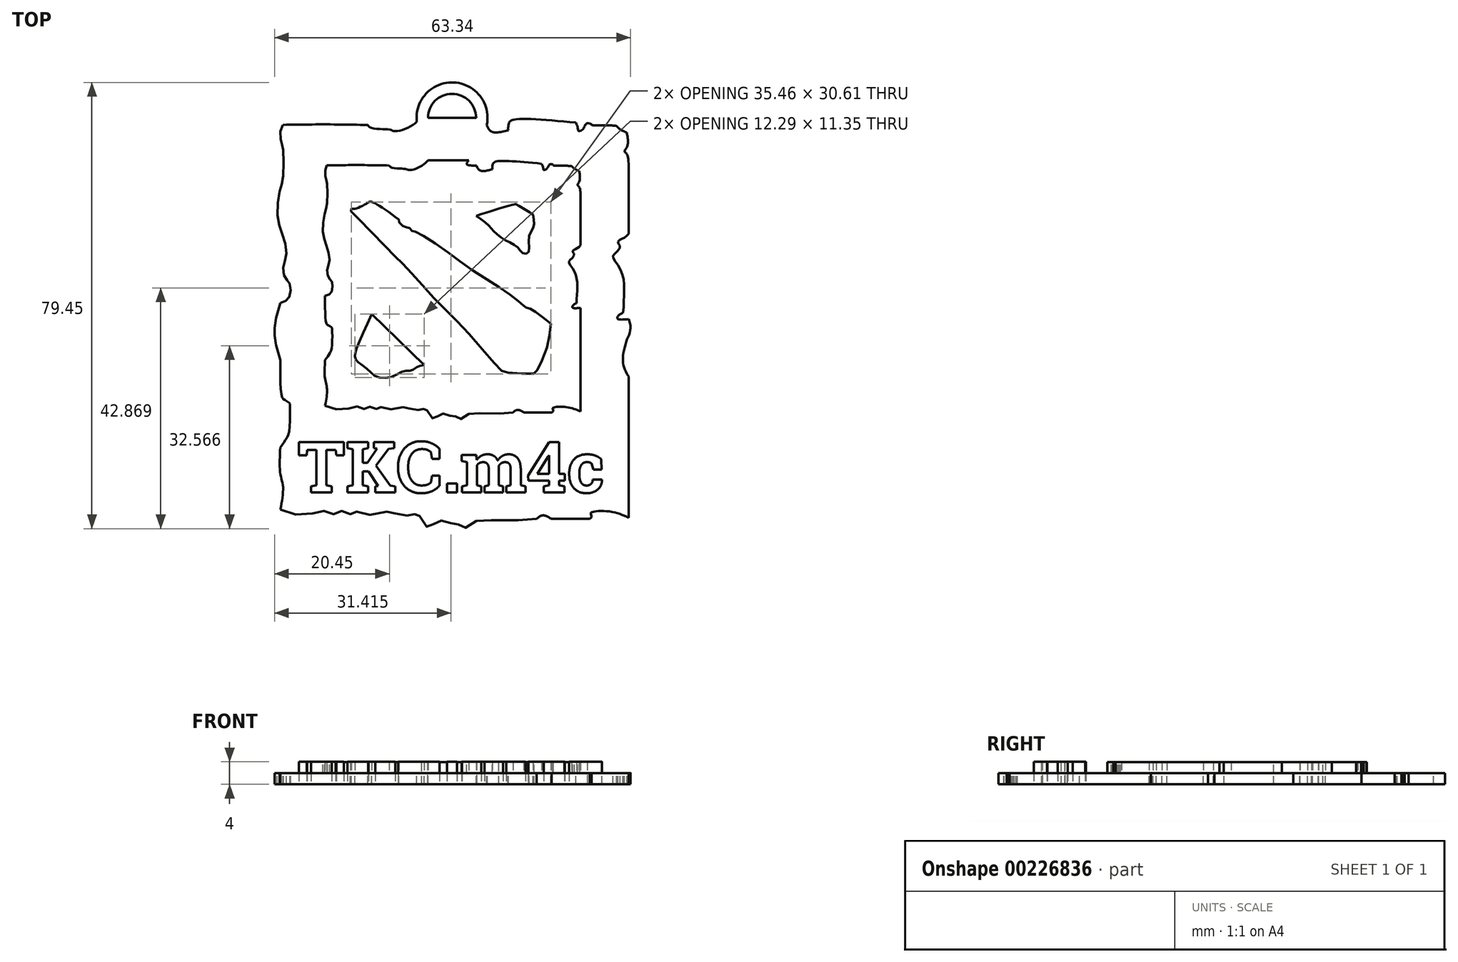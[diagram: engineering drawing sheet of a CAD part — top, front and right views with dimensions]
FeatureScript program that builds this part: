
annotation { "Feature Type Name" : "Feature", "Feature Type Description" : "" }
export const myFeature = defineFeature(function(context is Context, id is Id, definition is map)
    precondition{}
    {
        {
            var Q0;
            Q0=qCreatedBy(makeId("Top.planeOp"),FACE);
            var sketch = newSketch(context, id + "F0", { "sketchPlane" : qUnion([Q0])});
            skFitSpline(sketch, "E0", {"points": [v(-33.75, 32) * mm, v(-25.5, 32.08) * mm, v(-16.92, 31.97) * mm], "startDerivative": vector(16.6, 0.27) * mm, "endDerivative": vector(17.06, -0.32) * mm});
            skFitSpline(sketch, "E1", {"points": [v(-16.92, 31.97) * mm, v(-16.52, 31.48) * mm, v(-13.93, 31.14) * mm, v(-12.41, 31) * mm, v(-11.9, 30.8) * mm, v(-10.5, 30.89) * mm, v(-8.07, 31.97) * mm, v(-6.47, 33.38) * mm], "startDerivative": vector(2.54, -5.86) * mm, "endDerivative": vector(8.52, 8.71) * mm});
            skFitSpline(sketch, "E2", {"points": [v(-6.47, 33.38) * mm, v(-1.08, 33.38) * mm, v(4.48, 33.38) * mm], "startDerivative": vector(10.82, 0) * mm, "endDerivative": vector(11.07, 0) * mm});
            skFitSpline(sketch, "E3", {"points": [v(4.48, 33.38) * mm, v(3.99, 32.57) * mm, v(4.12, 32.17) * mm, v(6.59, 31.97) * mm], "startDerivative": vector(-2.1, -2.8) * mm, "endDerivative": vector(6.43, 0.1) * mm});
            skFitSpline(sketch, "E4", {"points": [v(6.59, 31.97) * mm, v(6.99, 31.13) * mm, v(7.92, 30.5) * mm, v(10.83, 30.93) * mm], "startDerivative": vector(1.26, -3.38) * mm, "endDerivative": vector(7.2, 1.84) * mm});
            skFitSpline(sketch, "E5", {"points": [v(10.83, 30.93) * mm, v(10.83, 31.73) * mm, v(11.08, 32.55) * mm, v(12.23, 33.1) * mm, v(24.17, 32.44) * mm], "startDerivative": vector(-0.26, 5.62) * mm, "endDerivative": vector(27.71, -2.66) * mm});
            skFitSpline(sketch, "E6", {"points": [v(24.17, 32.44) * mm, v(24.5, 31.65) * mm, v(24.62, 30.93) * mm, v(24.77, 30.75) * mm, v(25.5, 31.08) * mm, v(25.97, 31.86) * mm, v(26.34, 32.26) * mm, v(27.18, 32.22) * mm], "startDerivative": vector(2.46, -4.74) * mm, "endDerivative": vector(5.95, -1.14) * mm});
            skFitSpline(sketch, "E7", {"points": [v(27.18, 32.22) * mm, v(27.33, 31.98) * mm, v(29.8, 31.92) * mm, v(32.24, 31.79) * mm], "startDerivative": vector(0.37, -1.86) * mm, "endDerivative": vector(5.24, -0.52) * mm});
            skFitSpline(sketch, "E8", {"points": [v(32.24, 31.79) * mm, v(33.09, 31.03) * mm, v(34.27, 30.47) * mm], "startDerivative": vector(1.63, -1.69) * mm, "endDerivative": vector(2.43, -0.96) * mm});
            skFitSpline(sketch, "E9", {"points": [v(34.27, 30.47) * mm, v(34.45, 29.27) * mm, v(34.27, 27.58) * mm, v(33.81, 26.8) * mm, v(34.27, 26.18) * mm, v(34.61, 23.93) * mm], "startDerivative": vector(1.07, -5.78) * mm, "endDerivative": vector(0.21, -10.06) * mm});
            skFitSpline(sketch, "E10", {"points": [v(34.61, 23.93) * mm, v(34.61, 16.23) * mm, v(34.61, 10.43) * mm], "startDerivative": vector(0, -14.89) * mm, "endDerivative": vector(0, -12.03) * mm});
            skFitSpline(sketch, "E11", {"points": [v(34.61, 10.43) * mm, v(33.76, 9.64) * mm, v(32.84, 9.24) * mm, v(32.53, 8.72) * mm, v(32.94, 7.95) * mm, v(31.9, 6.53) * mm, v(31.52, 5.83) * mm, v(33, 3.4) * mm, v(33.75, -0.34) * mm, v(33.53, -5.2) * mm], "startDerivative": vector(-8.77, -10.02) * mm, "endDerivative": vector(-1.92, -26.87) * mm});
            skFitSpline(sketch, "E12", {"points": [v(33.53, -5.2) * mm, v(32.7, -5.62) * mm, v(32.42, -6.3) * mm, v(34.61, -6.44) * mm], "startDerivative": vector(-3.03, -0.99) * mm, "endDerivative": vector(6.73, 0.55) * mm});
            skLineSegment(sketch, "E13", {"start": v(34.61, -6.44) * mm, "end": v(34.61, -34.4) * mm});
            skFitSpline(sketch, "E14", {"points": [v(34.61, -34.4) * mm, v(31.49, -33.28) * mm, v(27.87, -33.17) * mm, v(27.13, -33.56) * mm, v(27.3, -34.13) * mm, v(26.95, -34.63) * mm], "startDerivative": vector(-9.89, 4.47) * mm, "endDerivative": vector(-4.32, -3.7) * mm});
            skLineSegment(sketch, "E15", {"start": v(26.95, -34.63) * mm, "end": v(19.36, -34.63) * mm});
            skFitSpline(sketch, "E16", {"points": [v(19.36, -34.63) * mm, v(17.7, -33.94) * mm, v(16.42, -34.63) * mm], "startDerivative": vector(-3.3, 2.04) * mm, "endDerivative": vector(-2.58, -2.11) * mm});
            skFitSpline(sketch, "E17", {"points": [v(16.42, -34.63) * mm, v(12.06, -34.93) * mm, v(5.14, -34.89) * mm, v(4.32, -35.14) * mm, v(2.54, -36.3) * mm, v(1.93, -36.57) * mm, v(1.03, -35.77) * mm, v(0.73, -35.41) * mm, v(-0.44, -35.52) * mm, v(-1.43, -35.12) * mm, v(-2.6, -34.97) * mm, v(-3.59, -35.22) * mm, v(-4.11, -36) * mm, v(-4.64, -36.5) * mm, v(-6.1, -35.27) * mm, v(-6.8, -33.88) * mm, v(-7.07, -33.53) * mm, v(-7.55, -33.55) * mm, v(-8.02, -34.18) * mm, v(-8.7, -33.99) * mm, v(-10.8, -33.97) * mm, v(-11.85, -33.3) * mm, v(-12.88, -33.13) * mm, v(-13.95, -33.55) * mm, v(-18.63, -33.59) * mm, v(-19.14, -33.17) * mm, v(-19.79, -33.19) * mm, v(-20.27, -33.63) * mm, v(-21.32, -33.59) * mm, v(-22.12, -33.1) * mm, v(-22.9, -33.37) * mm, v(-23.83, -33.72) * mm, v(-24.63, -33.34) * mm, v(-26.4, -33.06) * mm, v(-27.96, -33.61) * mm, v(-31.3, -33.74) * mm, v(-34.23, -32.79) * mm], "startDerivative": vector(-74.15, -8.25) * mm, "endDerivative": vector(-65.65, 27.85) * mm});
            skFitSpline(sketch, "E18", {"points": [v(-34.23, -32.79) * mm, v(-33.7, -28.36) * mm, v(-34.23, -25.66) * mm, v(-34.23, -20.5) * mm], "startDerivative": vector(2.68, 13.73) * mm, "endDerivative": vector(0.83, 15.08) * mm});
            skFitSpline(sketch, "E19", {"points": [v(-34.23, -20.5) * mm, v(-33.22, -19.04) * mm, v(-32.46, -17.21) * mm, v(-32.3, -12.27) * mm, v(-32.4, -11.77) * mm, v(-33.33, -11.13) * mm, v(-33.86, -10.63) * mm, v(-34.23, -3.23) * mm], "startDerivative": vector(8.07, 11.72) * mm, "endDerivative": vector(0.07, 36.72) * mm});
            skFitSpline(sketch, "E20", {"points": [v(-34.23, -3.23) * mm, v(-32.96, -2.72) * mm, v(-32.33, -1.61) * mm, v(-32.3, 0.42) * mm, v(-32.72, 1.06) * mm, v(-33.46, 2.12) * mm, v(-33.57, 4.34) * mm, v(-33.04, 6.34) * mm, v(-33.78, 10.26) * mm, v(-34.81, 13.93) * mm, v(-34.23, 19.37) * mm, v(-33.73, 21.46) * mm, v(-33.7, 27.54) * mm, v(-33.89, 28.1) * mm, v(-34.22, 29.92) * mm, v(-33.75, 32) * mm], "startDerivative": vector(27.07, 7.5) * mm, "endDerivative": vector(17.92, 26.14) * mm});
            skLineSegment(sketch, "E21", {"start": v(-21.63, -8.06) * mm, "end": v(-7.55, -21.87) * mm});
            skFitSpline(sketch, "E22", {"points": [v(-7.55, -21.87) * mm, v(-9.41, -22.38) * mm, v(-11.03, -23.36) * mm, v(-12.86, -23.48) * mm, v(-16.03, -24.94) * mm, v(-20.47, -24.94) * mm, v(-23.1, -22.72) * mm, v(-25.75, -20.68) * mm, v(-26.17, -19.55) * mm, v(-25.8, -17.63) * mm, v(-21.63, -8.06) * mm], "startDerivative": vector(-24.36, -3.93) * mm, "endDerivative": vector(28.42, 61.34) * mm});
            skFitSpline(sketch, "E23", {"points": [v(6.49, 18.38) * mm, v(9.94, 15.7) * mm, v(11.43, 14.03) * mm, v(14.5, 11.8) * mm, v(17.6, 9.96) * mm, v(19.11, 8.38) * mm, v(20.6, 8.57) * mm, v(20.73, 12.64) * mm, v(21.95, 15.45) * mm, v(21.82, 18.74) * mm], "startDerivative": vector(29.73, -21.03) * mm, "endDerivative": vector(-5.54, 30.41) * mm});
            skFitSpline(sketch, "E24", {"points": [v(21.82, 18.74) * mm, v(19.34, 20.29) * mm, v(17.34, 21.45) * mm, v(16.82, 21.52) * mm, v(6.49, 18.38) * mm], "startDerivative": vector(-10.21, 6.43) * mm, "endDerivative": vector(-30.39, -9.7) * mm});
            skFitSpline(sketch, "E25", {"points": [v(-27.11, 20.36) * mm, v(-25.97, 20.32) * mm, v(-22.88, 21.82) * mm, v(-21.63, 22.15) * mm, v(-14.34, 17.39) * mm], "startDerivative": vector(6.28, -1.6) * mm, "endDerivative": vector(21.31, -15.82) * mm});
            skFitSpline(sketch, "E26", {"points": [v(-14.34, 17.39) * mm, v(-14.34, 16.75) * mm, v(-12.52, 15.31) * mm, v(-11.77, 15.31) * mm, v(-10.88, 14.39) * mm, v(-9.75, 14.08) * mm, v(3.56, 5.09) * mm, v(5.92, 3.44) * mm, v(17.48, -4.25) * mm, v(19.84, -6.27) * mm, v(21.07, -6.68) * mm, v(26.61, -10.72) * mm], "startDerivative": vector(-5.12, -14.14) * mm, "endDerivative": vector(50.35, -40.82) * mm});
            skFitSpline(sketch, "E27", {"points": [v(26.61, -10.72) * mm, v(25.48, -17.52) * mm, v(22.91, -23.44) * mm, v(22.14, -24.16) * mm, v(14.66, -23.86) * mm, v(13.24, -23.28) * mm, v(4.52, -13.41) * mm, v(-4.7, -3.93) * mm, v(-12.6, 4.7) * mm, v(-17.29, 9.4) * mm, v(-26.8, 19.26) * mm, v(-27.38, 19.99) * mm, v(-27.11, 20.36) * mm], "startDerivative": vector(-5.7, -72.3) * mm, "endDerivative": vector(16.1, 15.96) * mm});
            skSolve(sketch);
        }
        {
            var Q0;
            Q0=qCreatedBy(makeId("Top.planeOp"),FACE);
            cPlane(context, id + "F1", {"entities" : qUnion([Q0]), "cplaneType" : CPlaneType.OFFSET, "offset" : 2 * mm, "oppositeDirection" : true, "width" : 150 * mm, "height" : 150 * mm});
        }
        {
            var Q0;
            Q0=qCreatedBy(id+"F1.planeOp",FACE);
            var sketch = newSketch(context, id + "F2", { "sketchPlane" : qUnion([Q0])});
            skText(sketch, "E28", { "text": "TKC.m4c", "fontName": "RobotoSlab-Bold.ttf"});
            const initialGuessF2  = {"E28": [-0.0275, -0.03612, 1, 0, 0.00912]};
            skSetInitialGuess(sketch, initialGuessF2);
            skSolve(sketch);
        }
        {
            var Q0;
            Q0=makeQuery(id+"F2.imprint","IMPRINT",FACE,{"disambiguationData":[TD([[makeQuery(id+"F2.imprint","IMPRINT",EDGE,{"derivedFrom":sQuery(id+"F2.wireOp",EDGE,"E28.sketch_text.stroke-0")}),-1.0]])]});
            var Q1;
            Q1=makeQuery(id+"F2.imprint","IMPRINT",FACE,{"disambiguationData":[TD([[makeQuery(id+"F2.imprint","IMPRINT",EDGE,{"derivedFrom":sQuery(id+"F2.wireOp",EDGE,"E28.sketch_text.stroke-16")}),-1.0]])]});
            var Q2;
            Q2=makeQuery(id+"F2.imprint","IMPRINT",FACE,{"disambiguationData":[TD([[makeQuery(id+"F2.imprint","IMPRINT",EDGE,{"derivedFrom":sQuery(id+"F2.wireOp",EDGE,"E28.sketch_text.stroke-45")}),-1.0]])]});
            var Q3;
            Q3=makeQuery(id+"F2.imprint","IMPRINT",FACE,{"disambiguationData":[TD([[makeQuery(id+"F2.imprint","IMPRINT",EDGE,{"derivedFrom":sQuery(id+"F2.wireOp",EDGE,"E28.sketch_text.stroke-69")}),-1.0]])]});
            var Q4;
            Q4=makeQuery(id+"F2.imprint","IMPRINT",FACE,{"disambiguationData":[TD([[makeQuery(id+"F2.imprint","IMPRINT",EDGE,{"derivedFrom":sQuery(id+"F2.wireOp",EDGE,"E28.sketch_text.stroke-73")}),-1.0]])]});
            var Q5;
            Q5=makeQuery(id+"F2.imprint","IMPRINT",FACE,{"disambiguationData":[TD([[makeQuery(id+"F2.imprint","IMPRINT",EDGE,{"derivedFrom":sQuery(id+"F2.wireOp",EDGE,"E28.sketch_text.stroke-116")}),-1.0]])]});
            var Q6;
            Q6=makeQuery(id+"F2.imprint","IMPRINT",FACE,{"disambiguationData":[TD([[makeQuery(id+"F2.imprint","IMPRINT",EDGE,{"derivedFrom":sQuery(id+"F2.wireOp",EDGE,"E28.sketch_text.stroke-136")}),-1.0]])]});
            extrude(context, id + "F3", {"entities" : qUnion([Q0, Q1, Q2, Q3, Q4, Q5, Q6]), "depth" : 4 * mm});
        }
        {
            var Q0;
            Q0=makeQuery(id+"F0.imprint","IMPRINT",FACE,{"disambiguationData":[TD([[makeQuery(id+"F0.imprint","IMPRINT",EDGE,{"derivedFrom":sQuery(id+"F0.wireOp",EDGE,"E0")}),-1.0]])]});
            extrude(context, id + "F4", {"entities" : qUnion([Q0]), "depth" : 3 * mm});
        }
        {
            var Q0;
            Q0=qCreatedBy(makeId("Top.planeOp"),FACE);
            var sketch = newSketch(context, id + "F5", { "sketchPlane" : qUnion([Q0])});
            skFitSpline(sketch, "E29", {"points": [v(-33.47, 32.6) * mm, v(-25.21, 32.68) * mm, v(-16.64, 32.57) * mm], "startDerivative": vector(16.6, 0.27) * mm, "endDerivative": vector(17.06, -0.32) * mm});
            skFitSpline(sketch, "E30", {"points": [v(-16.64, 32.57) * mm, v(-16.24, 32.08) * mm, v(-13.65, 31.73) * mm, v(-12.13, 31.6) * mm, v(-11.61, 31.4) * mm, v(-10.22, 31.48) * mm, v(-7.78, 32.57) * mm, v(-6.19, 33.98) * mm], "startDerivative": vector(2.54, -5.86) * mm, "endDerivative": vector(8.52, 8.71) * mm});
            skFitSpline(sketch, "E31", {"points": [v(-6.19, 33.98) * mm, v(-0.8, 33.98) * mm, v(4.76, 33.98) * mm], "startDerivative": vector(10.82, 0) * mm, "endDerivative": vector(11.07, 0) * mm});
            skFitSpline(sketch, "E32", {"points": [v(4.76, 33.98) * mm, v(4.27, 33.17) * mm, v(4.4, 32.77) * mm, v(6.87, 32.57) * mm], "startDerivative": vector(-2.1, -2.8) * mm, "endDerivative": vector(6.43, 0.1) * mm});
            skFitSpline(sketch, "E33", {"points": [v(6.87, 32.57) * mm, v(7.27, 31.73) * mm, v(8.2, 31.1) * mm, v(11.11, 31.53) * mm], "startDerivative": vector(1.26, -3.38) * mm, "endDerivative": vector(7.2, 1.84) * mm});
            skFitSpline(sketch, "E34", {"points": [v(11.11, 31.53) * mm, v(11.11, 32.33) * mm, v(11.36, 33.15) * mm, v(12.51, 33.7) * mm, v(24.45, 33.04) * mm], "startDerivative": vector(-0.26, 5.62) * mm, "endDerivative": vector(27.71, -2.66) * mm});
            skFitSpline(sketch, "E35", {"points": [v(24.45, 33.04) * mm, v(24.78, 32.25) * mm, v(24.9, 31.53) * mm, v(25.05, 31.35) * mm, v(25.79, 31.67) * mm, v(26.25, 32.46) * mm, v(26.62, 32.86) * mm, v(27.46, 32.82) * mm], "startDerivative": vector(2.46, -4.74) * mm, "endDerivative": vector(5.95, -1.14) * mm});
            skFitSpline(sketch, "E36", {"points": [v(27.46, 32.82) * mm, v(27.61, 32.58) * mm, v(30.07, 32.52) * mm, v(32.52, 32.39) * mm], "startDerivative": vector(0.37, -1.86) * mm, "endDerivative": vector(5.24, -0.52) * mm});
            skFitSpline(sketch, "E37", {"points": [v(32.52, 32.39) * mm, v(33.37, 31.63) * mm, v(34.55, 31.06) * mm], "startDerivative": vector(1.63, -1.69) * mm, "endDerivative": vector(2.43, -0.96) * mm});
            skFitSpline(sketch, "E38", {"points": [v(34.55, 31.06) * mm, v(34.73, 29.86) * mm, v(34.55, 28.17) * mm, v(34.1, 27.4) * mm, v(34.55, 26.78) * mm, v(34.9, 24.52) * mm], "startDerivative": vector(1.07, -5.78) * mm, "endDerivative": vector(0.21, -10.06) * mm});
            skFitSpline(sketch, "E39", {"points": [v(34.9, 24.52) * mm, v(34.9, 16.82) * mm, v(34.9, 11.03) * mm], "startDerivative": vector(0, -14.89) * mm, "endDerivative": vector(0, -12.03) * mm});
            skFitSpline(sketch, "E40", {"points": [v(34.9, 11.03) * mm, v(34.04, 10.24) * mm, v(33.12, 9.84) * mm, v(32.81, 9.31) * mm, v(33.22, 8.55) * mm, v(32.18, 7.13) * mm, v(31.8, 6.43) * mm, v(33.28, 4) * mm, v(34.03, 0.26) * mm, v(33.81, -4.6) * mm], "startDerivative": vector(-8.77, -10.02) * mm, "endDerivative": vector(-1.92, -26.87) * mm});
            skFitSpline(sketch, "E41", {"points": [v(33.81, -4.6) * mm, v(32.98, -5.02) * mm, v(32.7, -5.7) * mm, v(34.9, -5.85) * mm], "startDerivative": vector(-3.03, -0.99) * mm, "endDerivative": vector(6.73, 0.55) * mm});
            skLineSegment(sketch, "E42", {"start": v(34.9, -17.15) * mm, "end": v(34.9, -45.1) * mm});
            skFitSpline(sketch, "E43", {"points": [v(34.9, -45.1) * mm, v(31.77, -43.98) * mm, v(28.15, -43.87) * mm, v(27.41, -44.27) * mm, v(27.59, -44.83) * mm, v(27.23, -45.33) * mm], "startDerivative": vector(-9.89, 4.47) * mm, "endDerivative": vector(-4.32, -3.7) * mm});
            skLineSegment(sketch, "E44", {"start": v(27.23, -45.33) * mm, "end": v(19.64, -45.33) * mm});
            skFitSpline(sketch, "E45", {"points": [v(19.64, -45.33) * mm, v(17.97, -44.65) * mm, v(16.7, -45.33) * mm], "startDerivative": vector(-3.3, 2.04) * mm, "endDerivative": vector(-2.58, -2.11) * mm});
            skFitSpline(sketch, "E46", {"points": [v(16.7, -45.33) * mm, v(12.34, -45.63) * mm, v(5.42, -45.6) * mm, v(4.6, -45.84) * mm, v(2.82, -47) * mm, v(2.2, -47.27) * mm, v(1.3, -46.47) * mm, v(1.01, -46.12) * mm, v(-0.16, -46.22) * mm, v(-1.15, -45.82) * mm, v(-2.32, -45.68) * mm, v(-3.3, -45.93) * mm, v(-3.83, -46.7) * mm, v(-4.36, -47.2) * mm, v(-5.83, -45.97) * mm, v(-6.52, -44.59) * mm, v(-6.8, -44.23) * mm, v(-7.27, -44.25) * mm, v(-7.73, -44.88) * mm, v(-8.43, -44.7) * mm, v(-10.52, -44.67) * mm, v(-11.57, -44) * mm, v(-12.6, -43.83) * mm, v(-13.67, -44.25) * mm, v(-18.35, -44.3) * mm, v(-18.86, -43.87) * mm, v(-19.5, -43.9) * mm, v(-20, -44.34) * mm, v(-21.04, -44.3) * mm, v(-21.84, -43.8) * mm, v(-22.62, -44.07) * mm, v(-23.55, -44.42) * mm, v(-24.35, -44.05) * mm, v(-26.13, -43.76) * mm, v(-27.68, -44.31) * mm, v(-31.02, -44.45) * mm, v(-33.95, -43.5) * mm], "startDerivative": vector(-74.15, -8.25) * mm, "endDerivative": vector(-65.65, 27.85) * mm});
            skFitSpline(sketch, "E47", {"points": [v(-33.95, -43.5) * mm, v(-33.41, -39.07) * mm, v(-33.95, -36.36) * mm, v(-33.95, -31.2) * mm], "startDerivative": vector(2.68, 13.73) * mm, "endDerivative": vector(0.83, 15.08) * mm});
            skFitSpline(sketch, "E48", {"points": [v(-33.95, -31.2) * mm, v(-32.94, -29.74) * mm, v(-32.18, -27.92) * mm, v(-32.02, -22.97) * mm, v(-32.12, -22.47) * mm, v(-33.05, -21.84) * mm, v(-33.58, -21.33) * mm, v(-33.95, -13.93) * mm], "startDerivative": vector(8.07, 11.72) * mm, "endDerivative": vector(0.07, 36.72) * mm});
            skFitSpline(sketch, "E49", {"points": [v(-33.95, -2.63) * mm, v(-32.68, -2.12) * mm, v(-32.05, -1.01) * mm, v(-32.02, 1.02) * mm, v(-32.44, 1.66) * mm, v(-33.18, 2.71) * mm, v(-33.29, 4.93) * mm, v(-32.76, 6.94) * mm, v(-33.5, 10.85) * mm, v(-34.53, 14.53) * mm, v(-33.95, 19.97) * mm, v(-33.45, 22.06) * mm, v(-33.42, 28.14) * mm, v(-33.6, 28.7) * mm, v(-33.94, 30.52) * mm, v(-33.47, 32.6) * mm], "startDerivative": vector(27.07, 7.5) * mm, "endDerivative": vector(17.92, 26.14) * mm});
            skFitSpline(sketch, "E50", {"points": [v(-33.95, -13.93) * mm, v(-35.08, -8.31) * mm, v(-33.95, -2.63) * mm], "startDerivative": vector(-3.4, 11.26) * mm, "endDerivative": vector(3.4, 11.34) * mm});
            skFitSpline(sketch, "E51", {"points": [v(34.9, -5.85) * mm, v(34.66, -9.7) * mm, v(33.77, -13.93) * mm, v(34.9, -17.15) * mm], "startDerivative": vector(7.07, -16.27) * mm, "endDerivative": vector(7.32, -11.59) * mm});
            skSolve(sketch);
        }
        {
            var Q0;
            Q0=qCreatedBy(makeId("Top.planeOp"),FACE);
            var sketch = newSketch(context, id + "F6", { "sketchPlane" : qUnion([Q0])});
            skArc(sketch, "E52", {"start": v(6.87, 32.57) * mm, "mid": v(0.32, 40.99) * mm, "end": v(-6.97, 33.21) * mm});
            skArc(sketch, "E53", {"start": v(4.76, 33.98) * mm, "mid": v(0, 38.74) * mm, "end": v(-4.76, 33.98) * mm});
            skPoint(sketch, "E54", {"position": v(-6.97, 33.21) * mm});
            skPoint(sketch, "E55", {"position": v(-4.76, 33.98) * mm});
            skPoint(sketch, "E56", {"position": v(4.76, 33.98) * mm});
            skPoint(sketch, "E57", {"position": v(6.87, 32.57) * mm});
            skFitSpline(sketch, "E58", {"points": [v(-6.97, 33.21) * mm, v(-6.49, 31.83) * mm, v(-4.6, 32.43) * mm, v(-4.76, 33.98) * mm], "startDerivative": vector(0.27, -5.7) * mm, "endDerivative": vector(-2.15, 5.17) * mm});
            skFitSpline(sketch, "E59", {"points": [v(4.76, 33.98) * mm, v(2.84, 32.13) * mm, v(3.21, 30.1) * mm, v(6.88, 30.07) * mm, v(6.87, 32.57) * mm], "startDerivative": vector(-9.42, -6.53) * mm, "endDerivative": vector(-3.81, 12.24) * mm});
            skSolve(sketch);
        }
        {
            var Q0;
            Q0=makeQuery(id+"F5.imprint","IMPRINT",FACE,{"disambiguationData":[TD([[makeQuery(id+"F5.imprint","IMPRINT",EDGE,{"derivedFrom":sQuery(id+"F5.wireOp",EDGE,"E29")}),-1.0]])]});
            var Q1;
            Q1=makeQuery(id+"F6.imprint","IMPRINT",FACE,{"disambiguationData":[TD([[makeQuery(id+"F6.imprint","IMPRINT",EDGE,{"derivedFrom":sQuery(id+"F6.wireOp",EDGE,"E52")}),1.0]])]});
            extrude(context, id + "F7", {"entities" : qUnion([Q0, Q1]), "oppositeDirection" : true, "depth" : (2 / 0.9) * mm});
        }
        {
            var Q0;
            Q0=makeQuery(id+"F7.opExtrude","SWEPT_BODY",BODY,{"disambiguationData":[OSD([sQuery(id+"F5.wireOp",EDGE,"E29"),sQuery(id+"F5.wireOp",EDGE,"E30"),sQuery(id+"F5.wireOp",EDGE,"E31"),sQuery(id+"F5.wireOp",EDGE,"E32"),sQuery(id+"F5.wireOp",EDGE,"E33"),sQuery(id+"F5.wireOp",EDGE,"E34"),sQuery(id+"F5.wireOp",EDGE,"E35"),sQuery(id+"F5.wireOp",EDGE,"E36"),sQuery(id+"F5.wireOp",EDGE,"E37"),sQuery(id+"F5.wireOp",EDGE,"E38"),sQuery(id+"F5.wireOp",EDGE,"E39"),sQuery(id+"F5.wireOp",EDGE,"E40"),sQuery(id+"F5.wireOp",EDGE,"E41"),sQuery(id+"F5.wireOp",EDGE,"E42"),sQuery(id+"F5.wireOp",EDGE,"E43"),sQuery(id+"F5.wireOp",EDGE,"E44"),sQuery(id+"F5.wireOp",EDGE,"E45"),sQuery(id+"F5.wireOp",EDGE,"E46"),sQuery(id+"F5.wireOp",EDGE,"E47"),sQuery(id+"F5.wireOp",EDGE,"E48"),sQuery(id+"F5.wireOp",EDGE,"E49"),sQuery(id+"F5.wireOp",EDGE,"E50"),sQuery(id+"F5.wireOp",EDGE,"E51")])]});
            var Q1;
            Q1=makeQuery(id+"F7.opExtrude","SWEPT_BODY",BODY,{"disambiguationData":[OSD([sQuery(id+"F6.wireOp",EDGE,"E52"),sQuery(id+"F6.wireOp",EDGE,"E53"),sQuery(id+"F6.wireOp",EDGE,"E58"),sQuery(id+"F6.wireOp",EDGE,"E59")])]});
            booleanBodies(context, id + "F8", {"operationType" : BooleanOperationType.UNION, "tools" : qUnion([Q0, Q1])});
        }
        {
            var Q0;
            Q0=makeQuery(id+"F7.opExtrude","SWEPT_BODY",BODY,{"disambiguationData":[OSD([sQuery(id+"F5.wireOp",EDGE,"E29"),sQuery(id+"F5.wireOp",EDGE,"E30"),sQuery(id+"F5.wireOp",EDGE,"E31"),sQuery(id+"F5.wireOp",EDGE,"E32"),sQuery(id+"F5.wireOp",EDGE,"E33"),sQuery(id+"F5.wireOp",EDGE,"E34"),sQuery(id+"F5.wireOp",EDGE,"E35"),sQuery(id+"F5.wireOp",EDGE,"E36"),sQuery(id+"F5.wireOp",EDGE,"E37"),sQuery(id+"F5.wireOp",EDGE,"E38"),sQuery(id+"F5.wireOp",EDGE,"E39"),sQuery(id+"F5.wireOp",EDGE,"E40"),sQuery(id+"F5.wireOp",EDGE,"E41"),sQuery(id+"F5.wireOp",EDGE,"E42"),sQuery(id+"F5.wireOp",EDGE,"E43"),sQuery(id+"F5.wireOp",EDGE,"E44"),sQuery(id+"F5.wireOp",EDGE,"E45"),sQuery(id+"F5.wireOp",EDGE,"E46"),sQuery(id+"F5.wireOp",EDGE,"E47"),sQuery(id+"F5.wireOp",EDGE,"E48"),sQuery(id+"F5.wireOp",EDGE,"E49"),sQuery(id+"F5.wireOp",EDGE,"E50"),sQuery(id+"F5.wireOp",EDGE,"E51")])]});
            var Q1;
            Q1=qCreatedBy(makeId("Origin.pointOp"),VERTEX);
            transform(context, id + "F9", {"entities" : qUnion([Q0]), "transformType" : TransformType.SCALE_UNIFORMLY, "scale" : 0.9, "scalePoint" : qUnion([Q1]), "makeCopy" : false});
        }
        {
            var Q0;
            Q0=makeQuery(id+"F0.imprint","IMPRINT",FACE,{"disambiguationData":[TD([[makeQuery(id+"F0.imprint","IMPRINT",EDGE,{"derivedFrom":sQuery(id+"F0.wireOp",EDGE,"E23")}),1.0]])]});
            var Q1;
            Q1=makeQuery(id+"F0.imprint","IMPRINT",FACE,{"disambiguationData":[TD([[makeQuery(id+"F0.imprint","IMPRINT",EDGE,{"derivedFrom":sQuery(id+"F0.wireOp",EDGE,"E25")}),-1.0]])]});
            var Q2;
            Q2=makeQuery(id+"F0.imprint","IMPRINT",FACE,{"disambiguationData":[TD([[makeQuery(id+"F0.imprint","IMPRINT",EDGE,{"derivedFrom":sQuery(id+"F0.wireOp",EDGE,"E21")}),-1.0]])]});
            var Q3;
            Q3=makeQuery(id+"F8.opBoolean","MERGE",FACE,{"derivedFrom":[makeQuery(id+"F7.opExtrude","CAP_FACE",FACE,{"disambiguationData":[OSD([sQuery(id+"F5.wireOp",EDGE,"E29"),sQuery(id+"F5.wireOp",EDGE,"E30"),sQuery(id+"F5.wireOp",EDGE,"E31"),sQuery(id+"F5.wireOp",EDGE,"E32"),sQuery(id+"F5.wireOp",EDGE,"E33"),sQuery(id+"F5.wireOp",EDGE,"E34"),sQuery(id+"F5.wireOp",EDGE,"E35"),sQuery(id+"F5.wireOp",EDGE,"E36"),sQuery(id+"F5.wireOp",EDGE,"E37"),sQuery(id+"F5.wireOp",EDGE,"E38"),sQuery(id+"F5.wireOp",EDGE,"E39"),sQuery(id+"F5.wireOp",EDGE,"E40"),sQuery(id+"F5.wireOp",EDGE,"E41"),sQuery(id+"F5.wireOp",EDGE,"E42"),sQuery(id+"F5.wireOp",EDGE,"E43"),sQuery(id+"F5.wireOp",EDGE,"E44"),sQuery(id+"F5.wireOp",EDGE,"E45"),sQuery(id+"F5.wireOp",EDGE,"E46"),sQuery(id+"F5.wireOp",EDGE,"E47"),sQuery(id+"F5.wireOp",EDGE,"E48"),sQuery(id+"F5.wireOp",EDGE,"E49"),sQuery(id+"F5.wireOp",EDGE,"E50"),sQuery(id+"F5.wireOp",EDGE,"E51")])],"isStart":false}),makeQuery(id+"F7.opExtrude","CAP_FACE",FACE,{"disambiguationData":[OSD([sQuery(id+"F6.wireOp",EDGE,"E52"),sQuery(id+"F6.wireOp",EDGE,"E53"),sQuery(id+"F6.wireOp",EDGE,"E58"),sQuery(id+"F6.wireOp",EDGE,"E59")])],"isStart":false})]});
            extrude(context, id + "F10", {"entities" : qUnion([Q0, Q1, Q2]), "oppositeDirection" : true, "endBoundEntityFace" : qUnion([Q3]), "depth" : 25 * mm});
        }
        {
            var Q0;
            Q0=makeQuery(id+"F4.opExtrude","SWEPT_BODY",BODY,{"disambiguationData":[OSD([sQuery(id+"F0.wireOp",EDGE,"E0"),sQuery(id+"F0.wireOp",EDGE,"E1"),sQuery(id+"F0.wireOp",EDGE,"E2"),sQuery(id+"F0.wireOp",EDGE,"E3"),sQuery(id+"F0.wireOp",EDGE,"E4"),sQuery(id+"F0.wireOp",EDGE,"E5"),sQuery(id+"F0.wireOp",EDGE,"E6"),sQuery(id+"F0.wireOp",EDGE,"E7"),sQuery(id+"F0.wireOp",EDGE,"E8"),sQuery(id+"F0.wireOp",EDGE,"E9"),sQuery(id+"F0.wireOp",EDGE,"E10"),sQuery(id+"F0.wireOp",EDGE,"E11"),sQuery(id+"F0.wireOp",EDGE,"E12"),sQuery(id+"F0.wireOp",EDGE,"E13"),sQuery(id+"F0.wireOp",EDGE,"E14"),sQuery(id+"F0.wireOp",EDGE,"E15"),sQuery(id+"F0.wireOp",EDGE,"E16"),sQuery(id+"F0.wireOp",EDGE,"E17"),sQuery(id+"F0.wireOp",EDGE,"E18"),sQuery(id+"F0.wireOp",EDGE,"E19"),sQuery(id+"F0.wireOp",EDGE,"E20"),sQuery(id+"F0.wireOp",EDGE,"E21"),sQuery(id+"F0.wireOp",EDGE,"E22"),sQuery(id+"F0.wireOp",EDGE,"E23"),sQuery(id+"F0.wireOp",EDGE,"E24"),sQuery(id+"F0.wireOp",EDGE,"E25"),sQuery(id+"F0.wireOp",EDGE,"E26"),sQuery(id+"F0.wireOp",EDGE,"E27")])]});
            var Q1;
            Q1=makeQuery(id+"F10.opExtrude","SWEPT_BODY",BODY,{"disambiguationData":[OSD([sQuery(id+"F0.wireOp",EDGE,"E23"),sQuery(id+"F0.wireOp",EDGE,"E24")])]});
            var Q2;
            Q2=makeQuery(id+"F10.opExtrude","SWEPT_BODY",BODY,{"disambiguationData":[OSD([sQuery(id+"F0.wireOp",EDGE,"E25"),sQuery(id+"F0.wireOp",EDGE,"E26"),sQuery(id+"F0.wireOp",EDGE,"E27")])]});
            var Q3;
            Q3=makeQuery(id+"F10.opExtrude","SWEPT_BODY",BODY,{"disambiguationData":[OSD([sQuery(id+"F0.wireOp",EDGE,"E21"),sQuery(id+"F0.wireOp",EDGE,"E22")])]});
            var Q4;
            Q4=qCreatedBy(makeId("Origin.pointOp"),VERTEX);
            transform(context, id + "F11", {"entities" : qUnion([Q0, Q1, Q2, Q3]), "transformType" : TransformType.SCALE_UNIFORMLY, "scale" : 0.66, "scalePoint" : qUnion([Q4]), "makeCopy" : false});
        }
        {
            var Q0;
            Q0=makeQuery(id+"F4.opExtrude","SWEPT_BODY",BODY,{"disambiguationData":[OSD([sQuery(id+"F0.wireOp",EDGE,"E0"),sQuery(id+"F0.wireOp",EDGE,"E1"),sQuery(id+"F0.wireOp",EDGE,"E2"),sQuery(id+"F0.wireOp",EDGE,"E3"),sQuery(id+"F0.wireOp",EDGE,"E4"),sQuery(id+"F0.wireOp",EDGE,"E5"),sQuery(id+"F0.wireOp",EDGE,"E6"),sQuery(id+"F0.wireOp",EDGE,"E7"),sQuery(id+"F0.wireOp",EDGE,"E8"),sQuery(id+"F0.wireOp",EDGE,"E9"),sQuery(id+"F0.wireOp",EDGE,"E10"),sQuery(id+"F0.wireOp",EDGE,"E11"),sQuery(id+"F0.wireOp",EDGE,"E12"),sQuery(id+"F0.wireOp",EDGE,"E13"),sQuery(id+"F0.wireOp",EDGE,"E14"),sQuery(id+"F0.wireOp",EDGE,"E15"),sQuery(id+"F0.wireOp",EDGE,"E16"),sQuery(id+"F0.wireOp",EDGE,"E17"),sQuery(id+"F0.wireOp",EDGE,"E18"),sQuery(id+"F0.wireOp",EDGE,"E19"),sQuery(id+"F0.wireOp",EDGE,"E20"),sQuery(id+"F0.wireOp",EDGE,"E21"),sQuery(id+"F0.wireOp",EDGE,"E22"),sQuery(id+"F0.wireOp",EDGE,"E23"),sQuery(id+"F0.wireOp",EDGE,"E24"),sQuery(id+"F0.wireOp",EDGE,"E25"),sQuery(id+"F0.wireOp",EDGE,"E26"),sQuery(id+"F0.wireOp",EDGE,"E27")])]});
            var Q1;
            Q1=makeQuery(id+"F10.opExtrude","SWEPT_BODY",BODY,{"disambiguationData":[OSD([sQuery(id+"F0.wireOp",EDGE,"E23"),sQuery(id+"F0.wireOp",EDGE,"E24")])]});
            var Q2;
            Q2=makeQuery(id+"F10.opExtrude","SWEPT_BODY",BODY,{"disambiguationData":[OSD([sQuery(id+"F0.wireOp",EDGE,"E25"),sQuery(id+"F0.wireOp",EDGE,"E26"),sQuery(id+"F0.wireOp",EDGE,"E27")])]});
            var Q3;
            Q3=makeQuery(id+"F10.opExtrude","SWEPT_BODY",BODY,{"disambiguationData":[OSD([sQuery(id+"F0.wireOp",EDGE,"E21"),sQuery(id+"F0.wireOp",EDGE,"E22")])]});
            transform(context, id + "F12", {"entities" : qUnion([Q0, Q1, Q2, Q3]), "transformType" : TransformType.TRANSLATION_3D, "dx" : 0 * mm, "dy" : 1 * mm, "dz" : 0 * mm, "makeCopy" : false});
        }
        {
            var Q0;
            Q0=makeQuery(id+"F10.opExtrude","SWEPT_BODY",BODY,{"disambiguationData":[OSD([sQuery(id+"F0.wireOp",EDGE,"E23"),sQuery(id+"F0.wireOp",EDGE,"E24")])]});
            var Q1;
            Q1=makeQuery(id+"F10.opExtrude","SWEPT_BODY",BODY,{"disambiguationData":[OSD([sQuery(id+"F0.wireOp",EDGE,"E25"),sQuery(id+"F0.wireOp",EDGE,"E26"),sQuery(id+"F0.wireOp",EDGE,"E27")])]});
            var Q2;
            Q2=makeQuery(id+"F10.opExtrude","SWEPT_BODY",BODY,{"disambiguationData":[OSD([sQuery(id+"F0.wireOp",EDGE,"E21"),sQuery(id+"F0.wireOp",EDGE,"E22")])]});
            var Q3;
            Q3=makeQuery(id+"F7.opExtrude","SWEPT_BODY",BODY,{"disambiguationData":[OSD([sQuery(id+"F5.wireOp",EDGE,"E29"),sQuery(id+"F5.wireOp",EDGE,"E30"),sQuery(id+"F5.wireOp",EDGE,"E31"),sQuery(id+"F5.wireOp",EDGE,"E32"),sQuery(id+"F5.wireOp",EDGE,"E33"),sQuery(id+"F5.wireOp",EDGE,"E34"),sQuery(id+"F5.wireOp",EDGE,"E35"),sQuery(id+"F5.wireOp",EDGE,"E36"),sQuery(id+"F5.wireOp",EDGE,"E37"),sQuery(id+"F5.wireOp",EDGE,"E38"),sQuery(id+"F5.wireOp",EDGE,"E39"),sQuery(id+"F5.wireOp",EDGE,"E40"),sQuery(id+"F5.wireOp",EDGE,"E41"),sQuery(id+"F5.wireOp",EDGE,"E42"),sQuery(id+"F5.wireOp",EDGE,"E43"),sQuery(id+"F5.wireOp",EDGE,"E44"),sQuery(id+"F5.wireOp",EDGE,"E45"),sQuery(id+"F5.wireOp",EDGE,"E46"),sQuery(id+"F5.wireOp",EDGE,"E47"),sQuery(id+"F5.wireOp",EDGE,"E48"),sQuery(id+"F5.wireOp",EDGE,"E49"),sQuery(id+"F5.wireOp",EDGE,"E50"),sQuery(id+"F5.wireOp",EDGE,"E51")])]});
            booleanBodies(context, id + "F13", {"operationType" : BooleanOperationType.SUBTRACTION, "tools" : qUnion([Q0, Q1, Q2]), "targets" : qUnion([Q3])});
        }
    });
